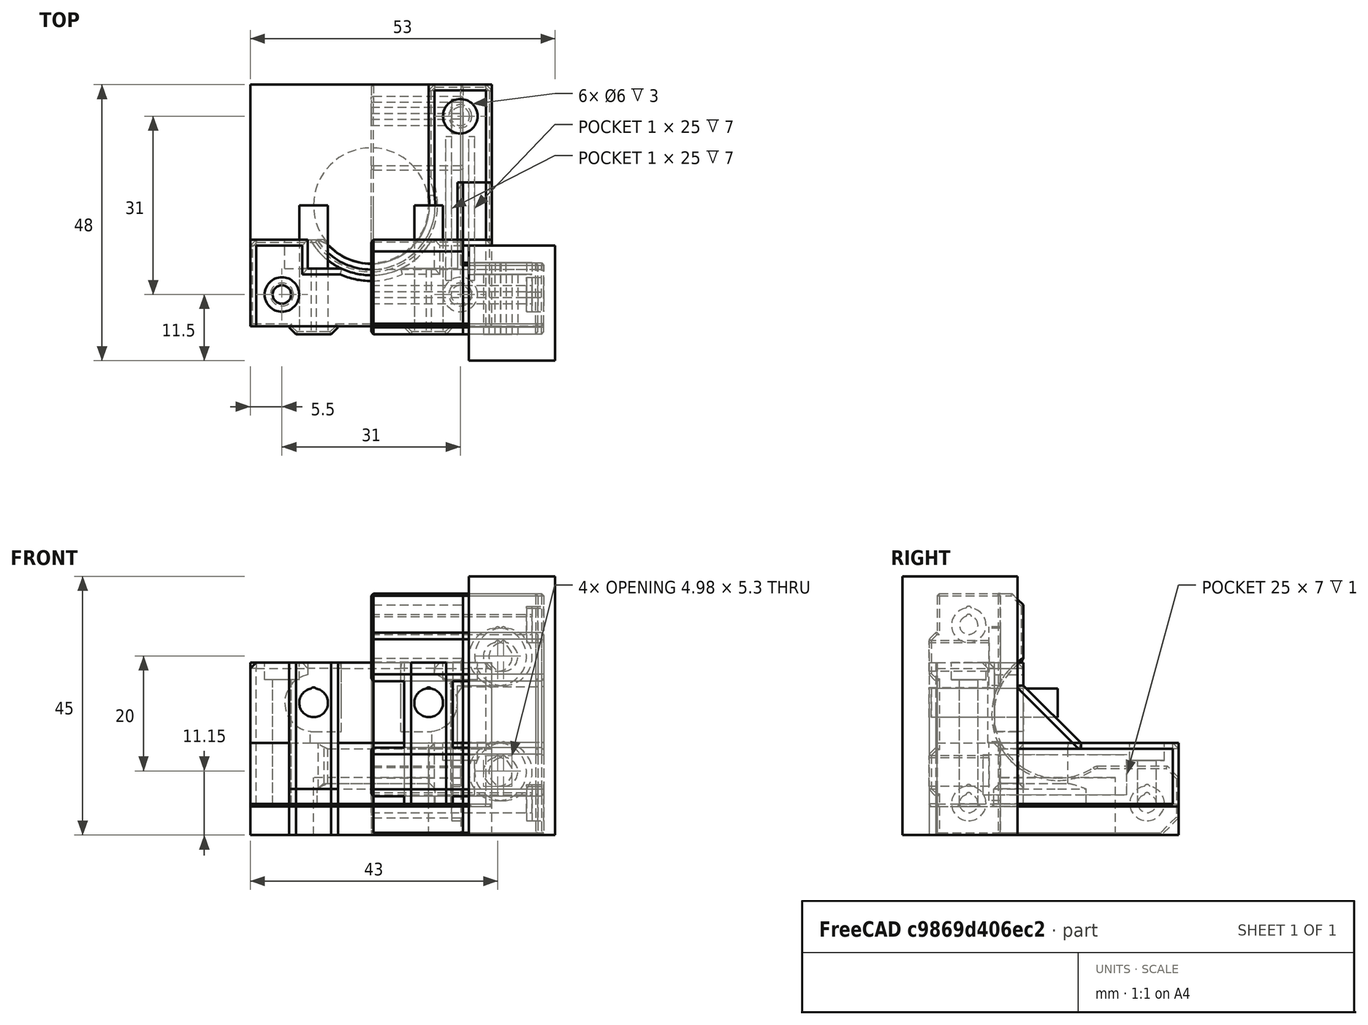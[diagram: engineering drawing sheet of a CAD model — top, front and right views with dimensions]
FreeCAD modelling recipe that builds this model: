
FCSTD DOCUMENT  (FreeCAD 0.18R14555 (Git shallow))
Label: y-motor-mount-10mm-lower
License: All rights reserved
LicenseURL: http://en.wikipedia.org/wiki/All_rights_reserved
objects: Part::Cylinder×20, Part::Box×16, Part::MultiFuse×15, Part::Feature×10, Part::Cut×10, Part::Chamfer×6, Part::MultiCommon×2, Part::Fillet×2
note: 81 computed .brp shape members not serialized (recipe doc carries the construction recipe); baked Part::Feature solids carry a one-line shape summary decoded from their .brp

FEATURE [Part::Box] Box  label="Cube"
  AttacherType = Attacher::AttachEngine3D
  Height = 16
  Length = 42
  Placement = pos=(-21,-21,0) rot=(0,0,1;0rad)
  Width = 42
FEATURE [Part::Cylinder] Cylinder
  Angle = 360
  AttacherType = Attacher::AttachEngine3D
  Height = 4
  Radius = 11.15
FEATURE [Part::Cylinder] Cylinder001
  Angle = 360
  AttacherType = Attacher::AttachEngine3D
  Height = 5
  Placement = pos=(-15.5,-15.5,28) rot=(0,0,1;0rad)
  Radius = 3
FEATURE [Part::Cylinder] Cylinder002
  Angle = 360
  AttacherType = Attacher::AttachEngine3D
  Height = 5
  Placement = pos=(15.5,15.5,13) rot=(0,0,1;0rad)
  Radius = 3
FEATURE [Part::Cylinder] Cylinder003
  Angle = 360
  AttacherType = Attacher::AttachEngine3D
  Height = 5
  Placement = pos=(15.5,-15.5,28) rot=(0,0,1;0rad)
  Radius = 3
FEATURE [Part::Box] Box001  label="Cube001"
  AttacherType = Attacher::AttachEngine3D
  Height = 30
  Length = 42
  Placement = pos=(-21,-21,0) rot=(0,0,1;0rad)
  Width = 15
FEATURE [Part::Box] Box002  label="Cube002"
  AttacherType = Attacher::AttachEngine3D
  Height = 16
  Length = 11
  Placement = pos=(10,-21,0) rot=(0,0,1;0rad)
  Width = 42
FEATURE [Part::Box] Box003  label="Cube003"
  AttacherType = Attacher::AttachEngine3D
  Height = 16
  Length = 42
  Placement = pos=(-21,-21,0) rot=(0,0,1;0rad)
  Width = 15
FEATURE [Part::Cylinder] Cylinder006
  Angle = 360
  AttacherType = Attacher::AttachEngine3D
  Height = 40
  Placement = pos=(-15.5,-15.5,0) rot=(0,0,1;0rad)
  Radius = 1.6
FEATURE [Part::Cylinder] Cylinder007
  Angle = 360
  AttacherType = Attacher::AttachEngine3D
  Height = 40
  Placement = pos=(15.5,-15.5,0) rot=(0,0,1;0rad)
  Radius = 1.6
FEATURE [Part::Cylinder] Cylinder008
  Angle = 360
  AttacherType = Attacher::AttachEngine3D
  Height = 40
  Placement = pos=(15.5,15.5,0) rot=(0,0,1;0rad)
  Radius = 1.6
FEATURE [Part::MultiFuse] Fusion001
  Shapes = -> [Cylinder006,Cylinder007,Cylinder008]
FEATURE [Part::Cylinder] Cylinder011
  Angle = 360
  AttacherType = Attacher::AttachEngine3D
  Height = 22
  Placement = pos=(-10,5.1e-15,23) rot=(1,0,0;1.5708rad)
  Radius = 2.5
FEATURE [Part::Cylinder] Cylinder012
  Angle = 360
  AttacherType = Attacher::AttachEngine3D
  Height = 10
  Placement = pos=(10,-10,23) rot=(1,0,0;1.5708rad)
  Radius = 5
FEATURE [Part::Cylinder] Cylinder013
  Angle = 360
  AttacherType = Attacher::AttachEngine3D
  Height = 22
  Placement = pos=(10,5.1e-15,23) rot=(1,0,0;1.5708rad)
  Radius = 2.5
FEATURE [Part::Cylinder] Cylinder014
  Angle = 360
  AttacherType = Attacher::AttachEngine3D
  Height = 10
  Placement = pos=(-10,-10,23) rot=(1,0,0;1.5708rad)
  Radius = 5
FEATURE [Part::MultiFuse] Fusion003
  Shapes = -> [Cylinder013,Cylinder011]
FEATURE [Part::Feature] Part__Feature  label="y_motor_mount v18"
  shape: bbox 62 x 21 x 44 mm, 162 faces (baked)
FEATURE [Part::Box] Box004  label="Cube004"
  AttacherType = Attacher::AttachEngine3D
  Height = 10
  Length = 10
  Placement = pos=(-15.5,-6,8) rot=(0,0,1;0rad)
  Width = 8
FEATURE [Part::MultiCommon] Common
  Placement = pos=(3.5,-15.5,2) rot=(0.57735,0.57735,-0.57735;4.18879rad)
  Shapes = -> [Part__Feature,Box004]
FEATURE [Part::Feature] Common001
  Placement = pos=(3.5,-15.5,2) rot=(0.57735,0.57735,-0.57735;4.18879rad)
  shape: bbox 8.45 x 1.4 x 8 mm, 8 faces (baked)
FEATURE [Part::Feature] Common002
  Placement = pos=(3.5,-15.5,24) rot=(0.57735,0.57735,-0.57735;4.18879rad)
  shape: bbox 8.45 x 1.4 x 8 mm, 8 faces (baked)
FEATURE [Part::Feature] Common003
  Placement = pos=(3.5,-15.5,16) rot=(0.57735,0.57735,-0.57735;4.18879rad)
  shape: bbox 8.45 x 1.4 x 8 mm, 8 faces (baked)
FEATURE [Part::Feature] Common004
  Placement = pos=(3.5,-15.5,9) rot=(0.57735,0.57735,-0.57735;4.18879rad)
  shape: bbox 8.45 x 1.4 x 8 mm, 8 faces (baked)
FEATURE [Part::MultiFuse] Fusion005
  Shapes = -> [Common002,Common003,Common004,Common001]
FEATURE [Part::Feature] Fusion005001  label="Fusion006"
  shape: bbox 8.45 x 1.4 x 30 mm, 8 faces (baked)
FEATURE [Part::Feature] Fusion005002  label="Fusion007"
  Placement = pos=(19.995,0,0) rot=(0,0,1;0rad)
  shape: bbox 8.45 x 1.4 x 30 mm, 8 faces (baked)
FEATURE [Part::Cylinder] Cylinder021
  Angle = 360
  AttacherType = Attacher::AttachEngine3D
  Height = 30
  Placement = pos=(10,0,0) rot=(1,0,0;1.5708rad)
  Radius = 2.5
FEATURE [Part::Cylinder] Cylinder022
  Angle = 360
  AttacherType = Attacher::AttachEngine3D
  Height = 30
  Placement = pos=(-10,0,0) rot=(1,0,0;1.5708rad)
  Radius = 2.5
FEATURE [Part::Feature] Chamfer002001  label="Chamfer003"
  Placement = pos=(-5e-15,0,21) rot=(0,1,0;1.5708rad)
  shape: bbox 30.28 x 43.4 x 42 mm, 123 faces (baked)
FEATURE [Part::Box] Box005  label="Cube005"
  AttacherType = Attacher::AttachEngine3D
  Height = 45
  Length = 15
  Placement = pos=(17,-27,0) rot=(0,0,1;0rad)
  Width = 20
FEATURE [Part::Feature] Chamfer002002  label="Chamfer004"
  Placement = pos=(-5e-15,0,21) rot=(0,1,0;1.5708rad)
  shape: bbox 30.28 x 43.4 x 42 mm, 123 faces (baked)
FEATURE [Part::Box] Box006  label="Cube006"
  AttacherType = Attacher::AttachEngine3D
  Height = 45
  Length = 15
  Placement = pos=(17,-27,0) rot=(0,0,1;0rad)
  Width = 20
FEATURE [Part::MultiCommon] Common005
  Placement = pos=(-1,0,0) rot=(0,0,1;0rad)
  Shapes = -> [Box006,Chamfer002002]
FEATURE [Part::Cylinder] Cylinder023
  Angle = 360
  AttacherType = Attacher::AttachEngine3D
  Height = 30
  Radius = 10.15
FEATURE [Part::MultiFuse] Fusion005006
  Shapes = -> [Cylinder023,Cylinder]
FEATURE [Part::Chamfer] Chamfer002003
  Base = -> Fusion005006
  Edges = 1 edges r=0.99: [Edge4]
  Placement = pos=(0,0,5) rot=(0,0,1;0rad)
FEATURE [Part::Cylinder] Cylinder024
  Angle = 360
  AttacherType = Attacher::AttachEngine3D
  Height = 39
  Radius = 12.15
FEATURE [Part::Cut] Cut
  Base = -> Box001
  Tool = -> Cylinder024
FEATURE [Part::Cylinder] Cylinder025
  Angle = 360
  AttacherType = Attacher::AttachEngine3D
  Height = 10
  Radius = 10
FEATURE [Part::MultiFuse] Fusion
  Shapes = -> [Box002,Box003]
FEATURE [Part::Chamfer] Chamfer
  Base = -> Fusion
  Edges = 1 edges r=5: [Edge17]
FEATURE [Part::MultiFuse] Fusion005003
  Placement = pos=(0,0,23) rot=(0,0,1;0rad)
  Shapes = -> [Cylinder022,Cylinder021]
FEATURE [Part::Cylinder] Cylinder026
  Angle = 360
  AttacherType = Attacher::AttachEngine3D
  Height = 30
  Placement = pos=(10,-30,25.2) rot=(-1,0,0;1.5708rad)
  Radius = 0.5
FEATURE [Part::Cylinder] Cylinder027
  Angle = 360
  AttacherType = Attacher::AttachEngine3D
  Height = 30
  Placement = pos=(-10,-30,25.2) rot=(-1,0,0;1.5708rad)
  Radius = 0.5
FEATURE [Part::Cylinder] Cylinder028
  Angle = 360
  AttacherType = Attacher::AttachEngine3D
  Height = 10
  Placement = pos=(10,-20,27.7) rot=(-1,0,0;1.5708rad)
  Radius = 0.5
FEATURE [Part::Cylinder] Cylinder029
  Angle = 360
  AttacherType = Attacher::AttachEngine3D
  Height = 10
  Placement = pos=(-10,-20,27.7) rot=(-1,0,0;1.5708rad)
  Radius = 0.5
FEATURE [Part::MultiFuse] Fusion005007
  Shapes = -> [Fusion005003,Cylinder026,Cylinder027]
FEATURE [Part::MultiFuse] Fusion005008
  Placement = pos=(0,9,0) rot=(0,0,1;0rad)
  Shapes = -> [Cylinder012,Cylinder028,Cylinder014,Cylinder029]
FEATURE [Part::MultiFuse] Fusion005010
  Placement = pos=(0,0,-1) rot=(0,0,1;0rad)
  Shapes = -> [Cylinder001,Cylinder003]
FEATURE [Part::MultiFuse] Fusion005011
  Shapes = -> [Chamfer,Cut,Fusion005001,Fusion005002]
FEATURE [Part::Box] Box007  label="Cube007"
  AttacherType = Attacher::AttachEngine3D
  Height = 5
  Length = 42
  Placement = pos=(-21,-26,0) rot=(0,0,1;0rad)
  Width = 47
FEATURE [Part::Cut] Cut001
  Base = -> Fusion005011
  Tool = -> Box007
FEATURE [Part::MultiFuse] Fusion005012
  Shapes = -> [Cylinder002,Fusion005010]
FEATURE [Part::Cut] Cut002
  Base = -> Cut001
  Tool = -> Fusion005012
FEATURE [Part::Cut] Cut003
  Base = -> Cut002
  Tool = -> Fusion001
FEATURE [Part::Cut] Cut004
  Base = -> Cut003
  Tool = -> Fusion005007
FEATURE [Part::Cut] Cut005
  Base = -> Cut004
  Tool = -> Fusion005008
FEATURE [Part::Cut] Cut006
  Base = -> Cut005
  Tool = -> Chamfer002003
FEATURE [Part::Box] Box008  label="Cube008"
  AttacherType = Attacher::AttachEngine3D
  Height = 16
  Length = 30
  Placement = pos=(-15,-11,18) rot=(0,0,1;0rad)
  Width = 10
FEATURE [Part::Fillet] Fillet
  Base = -> Box008
  Edges = 2 edges r=5: [Edge4,Edge8]
FEATURE [Part::Box] Box009  label="Cube009"
  AttacherType = Attacher::AttachEngine3D
  Height = 7
  Length = 3
  Placement = pos=(-11,-11,27) rot=(0,0,1;0rad)
  Width = 10
FEATURE [Part::Box] Box010  label="Cube010"
  AttacherType = Attacher::AttachEngine3D
  Height = 7
  Length = 3
  Placement = pos=(8,-11,27) rot=(0,0,1;0rad)
  Width = 10
FEATURE [Part::Box] Box011  label="Cube011"
  AttacherType = Attacher::AttachEngine3D
  Height = 6
  Length = 7
  Placement = pos=(8,-11,28) rot=(0,0,1;0rad)
  Width = 10
FEATURE [Part::Box] Box012  label="Cube012"
  AttacherType = Attacher::AttachEngine3D
  Height = 6
  Length = 7
  Placement = pos=(-15,-11,28) rot=(0,0,1;0rad)
  Width = 10
FEATURE [Part::MultiFuse] Fusion005013
  Shapes = -> [Box012,Box011]
FEATURE [Part::Cut] Cut007
  Base = -> Fillet
  Tool = -> Fusion005013
FEATURE [Part::Fillet] Fillet001
  Base = -> Cut007
  Edges = 2 edges r=4.99: [Edge2,Edge27]
FEATURE [Part::MultiFuse] Fusion005014
  Shapes = -> [Fillet001,Box009,Box010]
FEATURE [Part::Cut] Cut008
  Base = -> Cut006
  Tool = -> Fusion005014
FEATURE [Part::Box] Box013  label="Cube013"
  AttacherType = Attacher::AttachEngine3D
  Height = 11
  Length = 6
  Placement = pos=(15,-7,15) rot=(0,0,1;0rad)
  Width = 11
FEATURE [Part::Chamfer] Chamfer002004
  Base = -> Box013
  Edges = 1 edges r=10: [Edge12]
FEATURE [Part::Chamfer] Chamfer002005
  Base = -> Box013
  Edges = 1 edges r=10: [Edge12]
FEATURE [Part::MultiFuse] Fusion005015
  Shapes = -> [Chamfer002005,Cut008]
FEATURE [Part::Feature] Fusion005015001  label="Fusion005016"
  shape: bbox 42 x 43.4 x 25 mm, 55 faces (baked)
FEATURE [Part::Chamfer] Chamfer002006
  Base = -> Fusion005015001
  Edges = 22 edges r=1: [Edge15,Edge16,Edge23,Edge24,Edge90,Edge91,Edge92,Edge99,Edge111,Edge127,Edge132,Edge136,Edge137,Edge140,Edge142,Edge143,Edge145,Edge146,Edge147,Edge150,Edge153,Edge155]
FEATURE [Part::Chamfer] Chamfer002007
  Base = -> Chamfer002006
  Edges = 26 edges r=0.4: [Edge1,Edge8,Edge9,Edge10,Edge11,Edge12,Edge13,Edge14,Edge15,Edge16,Edge17,Edge18,Edge19,Edge20,Edge21,Edge22,Edge23,Edge24,Edge25,Edge26,Edge27,Edge28,Edge29,Edge30,Edge31,Edge32]
FEATURE [Part::Box] Box014  label="Cube014"
  AttacherType = Attacher::AttachEngine3D
  Height = 7
  Length = 1
  Placement = pos=(13,-13,7) rot=(0,0,1;0rad)
  Width = 25
FEATURE [Part::Box] Box015  label="Cube015"
  AttacherType = Attacher::AttachEngine3D
  Height = 7
  Length = 1
  Placement = pos=(17,-13,7) rot=(0,0,1;0rad)
  Width = 25
FEATURE [Part::MultiFuse] Fusion005015002  label="selective-infill"
  Shapes = -> [Box015,Box014]
FEATURE [Part::Cut] Cut009
  Base = -> Chamfer002007
  Tool = -> Fusion005015002
